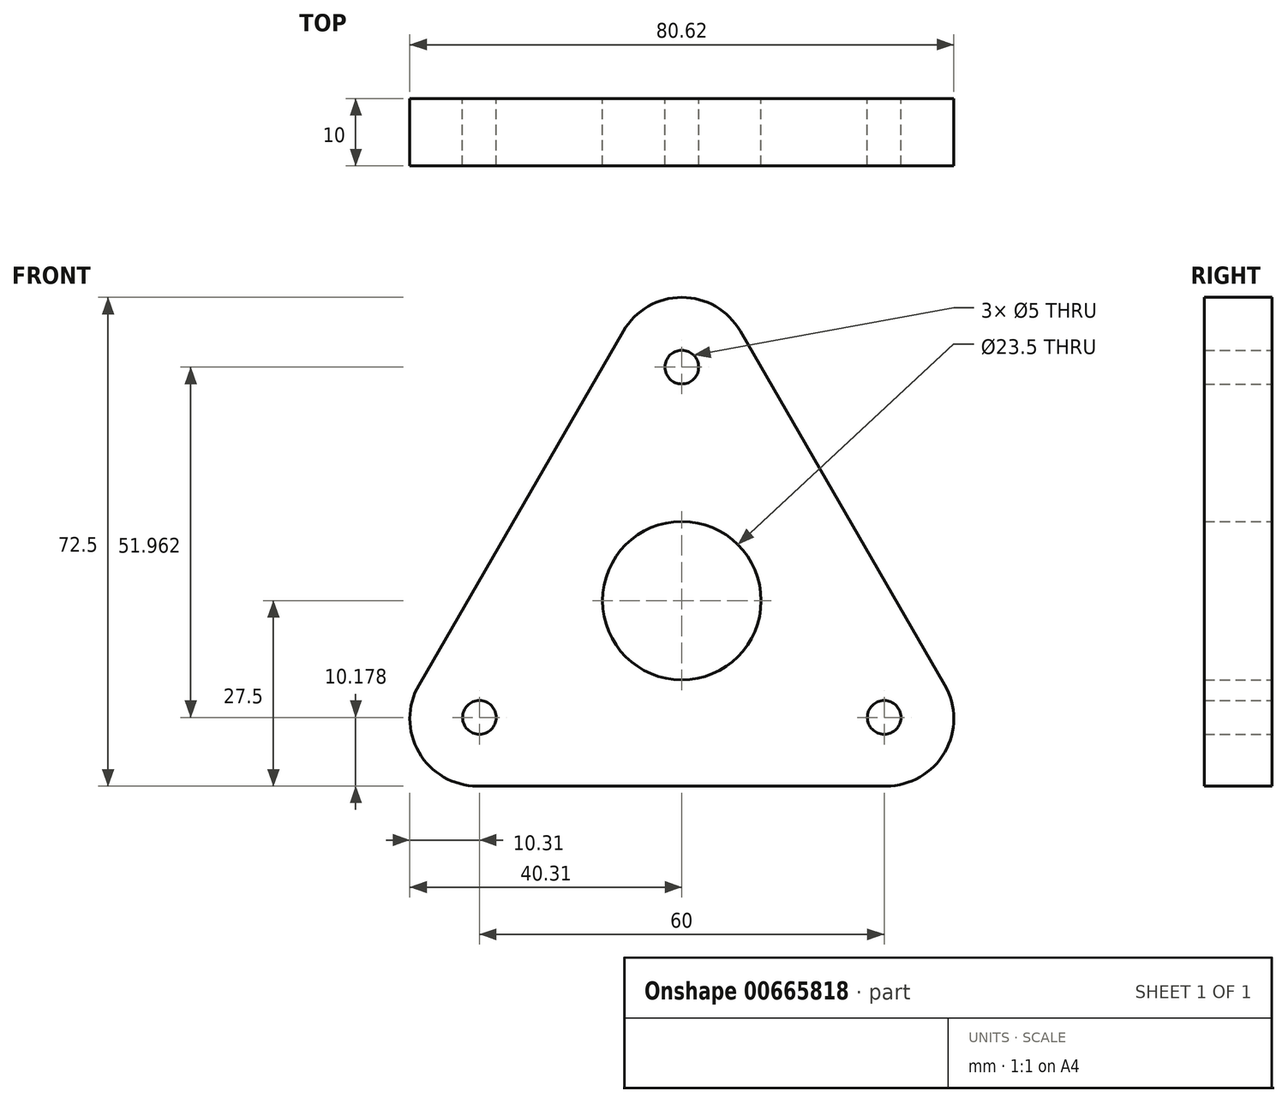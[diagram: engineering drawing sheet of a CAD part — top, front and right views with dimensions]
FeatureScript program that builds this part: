
annotation { "Feature Type Name" : "Feature", "Feature Type Description" : "" }
export const myFeature = defineFeature(function(context is Context, id is Id, definition is map)
    precondition{}
    {
        {
            var Q0;
            Q0=qCreatedBy(makeId("Front.planeOp"),FACE);
            var sketch = newSketch(context, id + "F0", { "sketchPlane" : qUnion([Q0])});
            skCircle(sketch, "E0", {"center": v(0, 0) * mm, "radius": 11.75 * mm});
            skCircle(sketch, "E1", {"center": v(0, 34.64) * mm, "radius": 2.5 * mm});
            skCircle(sketch, "E2", {"center": v(30, -17.32) * mm, "radius": 2.5 * mm});
            skCircle(sketch, "E3", {"center": v(-30, -17.32) * mm, "radius": 2.5 * mm});
            skCircle(sketch, "E4.cCircle", {"center": v(0, 0) * mm, "radius": 27.5 * mm, "construction": true});
            skLineSegment(sketch, "E4.0", {"start": v(30.31, -27.5) * mm, "end": v(-30.31, -27.5) * mm});
            skLineSegment(sketch, "E4.1", {"start": v(-38.97, -12.5) * mm, "end": v(-8.66, 40) * mm});
            skLineSegment(sketch, "E4.2", {"start": v(8.66, 40) * mm, "end": v(38.97, -12.5) * mm});
            skPoint(sketch, "E4.0.midPoint", {"position": v(0, -27.5) * mm});
            skPoint(sketch, "E5.visualSharp", {"position": v(0, 55) * mm});
            skArc(sketch, "E5.filletArc", {"start": v(8.66, 40) * mm, "mid": v(0, 45) * mm, "end": v(-8.66, 40) * mm});
            skPoint(sketch, "E6.visualSharp", {"position": v(-47.63, -27.5) * mm});
            skArc(sketch, "E6.filletArc", {"start": v(-38.97, -12.5) * mm, "mid": v(-38.97, -22.5) * mm, "end": v(-30.31, -27.5) * mm});
            skPoint(sketch, "E7.visualSharp", {"position": v(47.63, -27.5) * mm});
            skArc(sketch, "E7.filletArc", {"start": v(30.31, -27.5) * mm, "mid": v(38.97, -22.5) * mm, "end": v(38.97, -12.5) * mm});
            skSolve(sketch);
        }
        {
            var Q0;
            Q0=makeQuery(id+"F0.imprint","IMPRINT",FACE,{"disambiguationData":[TD([[makeQuery(id+"F0.imprint","IMPRINT",EDGE,{"derivedFrom":sQuery(id+"F0.wireOp",EDGE,"E0")}),-1.0]])]});
            extrude(context, id + "F1", {"entities" : qUnion([Q0]), "depth" : 10 * mm, "offsetDistance" : 25 * mm});
        }
    });
